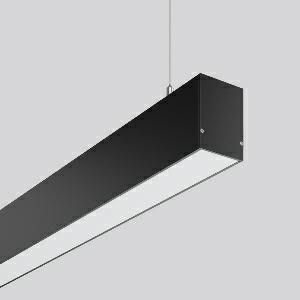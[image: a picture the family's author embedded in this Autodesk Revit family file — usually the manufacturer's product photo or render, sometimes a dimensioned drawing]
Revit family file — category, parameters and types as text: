
# Revit family: less_is_more_50_312319_003_76_c760
name_source: partatom
category: Lighting Fixtures
units: mm (PartAtom-declared; Revit-internal decimal feet)

## family parameters
Cut with Voids When Loaded = No
Host = Face
Light Source = No
Part Type = Normal
Room Calculation Point = No
Round Connector Dimension = Use Diameter
Shared = No

## types (1)
- LESS IS MORE 50 (1 x LED Modul 830, 6150 lm, 3000)
    Apparent Load = 52 VA
    CIE Flux Codes = 49 80 96 63 100
    Color Rendering = 80
    Color Temperature = 3000
    Default Elevation = 1800 mm
    Description = Series: LESS IS MORE 50
Linear pendant luminaire for aesthetically sophisticated lighting. Housing: extruded aluminium profile, powder-coated. End cap aluminium powder-coated. Canopy made of aluminium, powder-coated. Diffuser made of non-yellowing plastic (PMMA), opal. Direct 65%, indirect 35% light emission. Suitable for pendant. 2-point steel cable suspension freely positionable and infinitely height-adjustable. Special lengths available on request. LED unit with integrated converter interchangeable and removable. Suitable for through-wiring. With sensors or as a safety luminaire on request. 
Colour: deep black, matt (RAL 9005)
Length: 1407 mm
Width: 57 mm
Height: 75 mm
Suspension length: 2000 mm
Lamp: LED
Socket: without socket
Colour temperature: 3000K
Colour rendering index (CRI): 80
Light source: LED
Socket lamp2: Without base
Colour temperature: 3000K
System power: 52 W
Rated luminous flux: 6150 lm
Luminous efficiency: 118 lm/W
Control gear: Converter, dimmable, DALI
Control gear: Converter, dimmable, DALI
Protection class: I
Type of protection: IP 20
    Height = 75 mm
    Lamp = 1 x LED Modul 830
    Lamp Light Flux = 6150 lm
    Lamp count = 1
    Length = 1407 mm
    Lifetime = 50000 h
    Luminous efficacy = 118 lm/W
    Manufacturer = RZB
    ModVariant = No
    Model = 312319.003.76
    Mounting Place = Ceiling
    Mounting Type = Pendant
    Number of Poles = 1
    OnlyDefault = Yes
    Power Factor = 1
    Product Name = LESS IS MORE 50
    Product group = Pendant LED linear luminaires
    ProductGroupID = 907
    Protection Class = Protection class I
    Protection Degree = IP 20
    RLX_Detail_Level = 1
    RLX_Emergency_Light_Flux = 0 lm
    RLX_Emergency_Type = 0
    RLX_Emergency_Type_DB = No
    RlxData = <blob elided: 39901 chars, md5=801c73b4>
    Socket = socket
    Standby Power = 0 W
    System Light Flux = 6150 lm
    System Power = 52 W
    Type Comments = Product without accessories
    Type Image = 312318.003.jpg
    URL = http://relux.com
    VarID = ---
    Voltage = 230 V
    Voltage Range = 220-240 V
    Weight = 0.00 kg
    Width = 57 mm

## geometry (parser evidence)
native form markers: Blend x4, Sweep x11
no freeform markers — native parametric forms only
